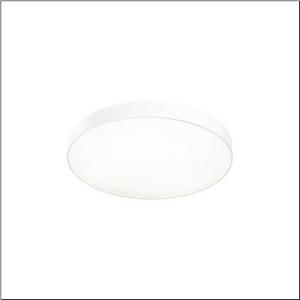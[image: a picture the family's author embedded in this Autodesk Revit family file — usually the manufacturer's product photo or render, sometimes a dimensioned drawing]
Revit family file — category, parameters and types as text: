
# Revit family: round_21_m_51mr36fd0321w
name_source: partatom
category: Lighting Fixtures
units: mm (PartAtom-declared; Revit-internal decimal feet)

## family parameters
Cut with Voids When Loaded = No
Host = Face
Light Source = No
Part Type = Normal
Room Calculation Point = No
Round Connector Dimension = Use Diameter
Shared = No

## types (1)
- Round 21 M (1 x LED, 7500 lm, 54.9 W, 3000K)
    Apparent Load = 55 VA
    CIE Flux Codes = 49 80 96 100 100
    Color Rendering = 80
    Color Temperature = 3000K
    Default Elevation = 1800 mm
    Description = Round 21 M, wall and ceiling luminaire, primary optical cover: cover, of PMMA, opal, light emission: direct distribution, primary light characteristic: symmetric, installation type: suspended mounting, surface-mounted, LED, rated luminous flux: 7.500lm, luminous efficacy: 137lm/W, light colour: 830, colour temperature: 3000K, control gear: DALI 2, with terminal, 5-pole, mains connection: 230V, AC, 50/60Hz, rated input power: 54.8W, housing, of aluminium, coated, white, diameter: 600mm, height: 62mm, protection rating (complete): IP40, insulation class (complete): insulation class I (protective earthing), certification: CE, impact resistance: IK04, permissible operating ambient temperature: -10..+35°C, packaging unit: 1 piece
    Height = 87 mm
    Lamp = 1 x LED
    Lamp Light Flux = 7500 lm
    Lamp Power = 54.9 W
    Lamp count = 1
    Length = 600 mm
    Luminous efficacy = 137 lm/W
    Manufacturer = Siteco
    ModVariant = No
    Model = 51MR36FD0321W
    Mounting Place = Ceiling
    Mounting Type = Surface mounted
    Number of Poles = 1
    OnlyDefault = Yes
    Power Factor = 1
    Product Name = Round 21 M
    Product group = wall and ceiling luminaire
    ProductGroupID = 304
    Protection Class = Protection class I
    Protection Degree = IP 40
    RLX_Detail_Level = 1
    RLX_Emergency_Light_Flux = 0 lm
    RLX_Emergency_Type = 0
    RLX_Emergency_Type_DB = No
    RlxData = <blob elided: 11721 chars, md5=235caf16>
    Socket = socket
    Standby Power = 0 W
    System Light Flux = 7500 lm
    System Power = 55 W
    Type Comments = Product without accessories
    Type Image = l_1258330.jpg
    URL = http://relux.com
    VarID = ---
    Voltage = 0 V
    Weight = 0.00 kg
    Width = 0 mm  [stored 0 ft]

note: [stored X ft] marks values corroborated as IEEE doubles in the binary element streams (Revit-internal decimal feet)

## geometry (parser evidence)
native form markers: Sweep x9
no freeform markers — native parametric forms only
